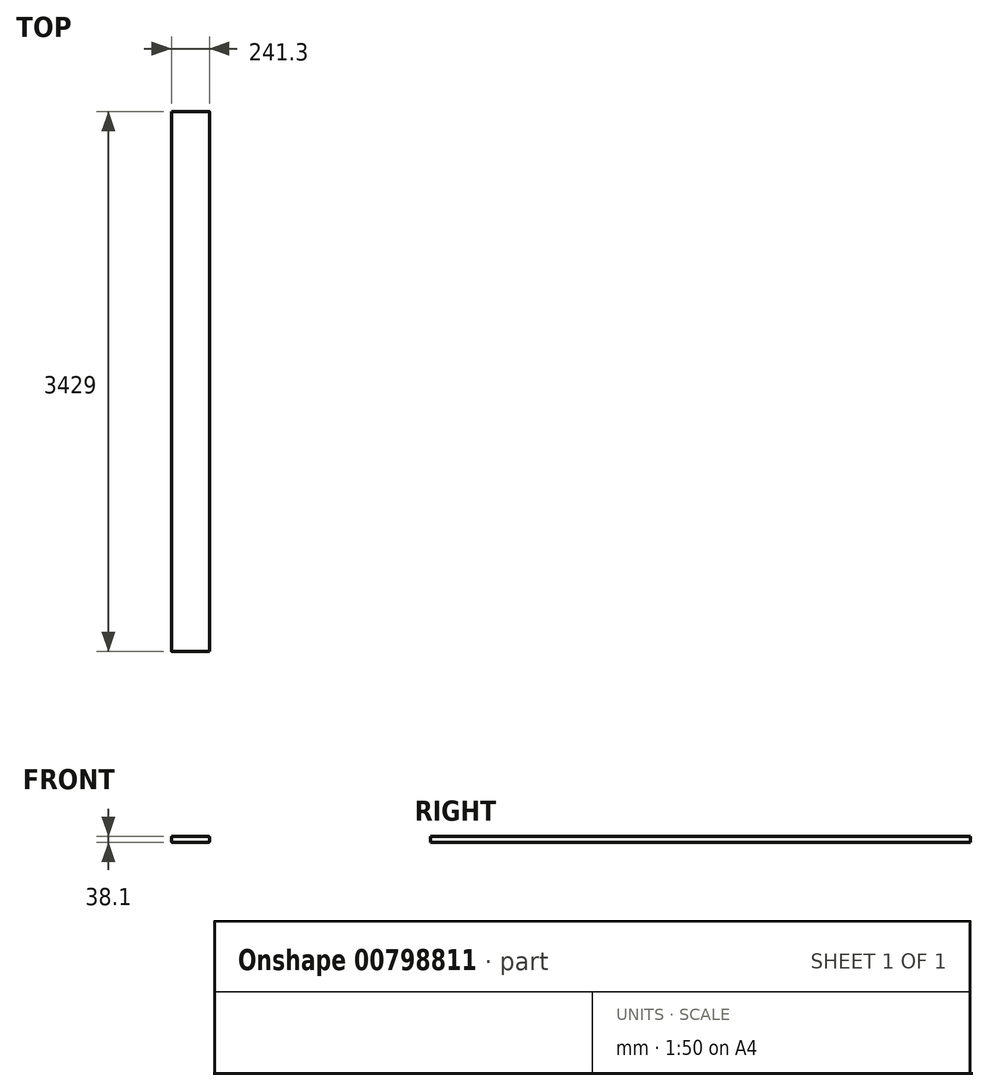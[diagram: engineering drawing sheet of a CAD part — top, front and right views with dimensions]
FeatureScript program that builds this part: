
annotation { "Feature Type Name" : "Feature", "Feature Type Description" : "" }
export const myFeature = defineFeature(function(context is Context, id is Id, definition is map)
    precondition{}
    {
        {
            var Q0;
            Q0=qCreatedBy(makeId("Front.planeOp"),FACE);
            var sketch = newSketch(context, id + "F0", { "sketchPlane" : qUnion([Q0])});
            skLineSegment(sketch, "E0.bottom", {"start": v(-115.82, 19.05) * mm, "end": v(115.82, 19.05) * mm});
            skLineSegment(sketch, "E0.top", {"start": v(-115.82, -19.05) * mm, "end": v(115.82, -19.05) * mm});
            skLineSegment(sketch, "E0.left", {"start": v(-120.65, 14.22) * mm, "end": v(-120.65, -14.22) * mm});
            skLineSegment(sketch, "E0.right", {"start": v(120.65, 14.22) * mm, "end": v(120.65, -14.22) * mm});
            skPoint(sketch, "E0.middle", {"position": v(0, 0) * mm});
            skPoint(sketch, "E1.visualSharp", {"position": v(-120.65, 19.05) * mm});
            skArc(sketch, "E1.filletArc", {"start": v(-115.82, 19.05) * mm, "mid": v(-119.24, 17.64) * mm, "end": v(-120.65, 14.22) * mm});
            skPoint(sketch, "E2.visualSharp", {"position": v(120.65, 19.05) * mm});
            skArc(sketch, "E2.filletArc", {"start": v(120.65, 14.22) * mm, "mid": v(119.24, 17.64) * mm, "end": v(115.82, 19.05) * mm});
            skPoint(sketch, "E3.visualSharp", {"position": v(120.65, -19.05) * mm});
            skArc(sketch, "E3.filletArc", {"start": v(115.82, -19.05) * mm, "mid": v(119.24, -17.64) * mm, "end": v(120.65, -14.22) * mm});
            skPoint(sketch, "E4.visualSharp", {"position": v(-120.65, -19.05) * mm});
            skArc(sketch, "E4.filletArc", {"start": v(-120.65, -14.22) * mm, "mid": v(-119.24, -17.64) * mm, "end": v(-115.82, -19.05) * mm});
            skSolve(sketch);
        }
        {
            var Q0;
            Q0=makeQuery(id+"F0.imprint","IMPRINT",FACE,{"disambiguationData":[TD([[makeQuery(id+"F0.imprint","IMPRINT",EDGE,{"derivedFrom":sQuery(id+"F0.wireOp",EDGE,"E0.bottom")}),-1.0]])]});
            extrude(context, id + "F1", {"entities" : qUnion([Q0]), "endBound" : BoundingType.SYMMETRIC, "depth" : 3429 * mm, "offsetDistance" : 25.4 * mm});
        }
    });
